# Revit family: Vitra-SinkMixer-Minimax S Series-A42091
name_source: partatom
category: Plumbing Fixtures
revit_build: Autodesk Revit 2017 (Build: 20160225_1515(x64)
units: mm (PartAtom-declared; Revit-internal decimal feet)

## family parameters
Cut with Voids When Loaded = No
Host = Face
OmniClass Number = 23.45.55.17
OmniClass Title = Mixing Faucets
Part Type = Normal
Room Calculation Point = No
Round Connector Dimension = Use Diameter
Shared = Yes

## types (1)
- SinkMixer-Vitra-MinimaxS Series-A42091
    Article No. (default) = A42091
    BIMobject category = Sink Mixer
    CW Connection = Yes
    Coating Material = Vitra-Chrome
    Color = Chrome
    Connection Diameter (mm) = 10 mm  [stored 0.0328084 ft]
    Cost = 0 $
    Default Elevation = 850 mm  [stored 2.78871 ft]
    Depth(mm) = 260 mm  [stored 0.853018 ft]
    Design country = Turkey
    HW Connection = Yes
    Height(mm) = 355 mm
    Hot Water Supply (max.) = 80 °C
    Hot Water temperature, factory set to = 38 °C
    IFC Classification = Sanitary Terminal
    Installation instructions = https://cdn.vitra.com.tr
    Main Material = Brass
    Manufacturer = Vitra
    Manufacturer name = Vitra
    Masterformat 2014 Code = 22 40 00
    Masterformat 2014 Description = Plumbing Fixtures
    Min. flow pressure of = 0.5 bar
    Model = A42091
    MountingType = Countertop
    NBS Referans Code = 45-35-70/345
    NBS Referans Description = Water supply fittings for sinks
    Nominal height = 0.000
    Nominal width = 0.000
    Number Of Connections = 2 mm  [stored 0.00656168 ft]
    OmniClass Code = 23.45.55.17
    OmniClass Description = Mixing Faucets
    Product Guid = https://cdn.vitra.com.tr
    Product Properties = Extra Water Saving, Green Building Certification, Energy Saving, Easy İnstallation
    Product SKU = A42091
    Product Type = Sink Mixer
    Product certification = https://vitraglobal.com
    Product data url = https://www.vitraglobal.com
    Product family = Minimax S
    Product group = Minimax S Sink Mixer
    Range of Hot Water Supply = 5 - 65 °C
    Range of flow pressure = 1 - 5 bar
    Technical description = https://www.vitraglobal.com
    Test Pressure = 16 bar
    UNSPSC Code = 301815
    URL = https://vitraglobal.com
    Uniclass 1.4 Code = L725111
    Uniclass 1.4 Description = Sink Mixer
    Uniclass 2.0 Code = Pr_40_30_96_47
    Uniclass 2.0 Description = Kitchen Taps
    Uniclass 2015 Code = Pr_40_20_87_84
    Uniclass 2015 Name = Sink taps
    Uniformat II Code = 22 40 00
    Uniformat II Description = Plumbing Fixture
    Warranty Period (Year) = 10 Years
    Weight Net (kg) = 1,524
    Width(mm) = 134 mm
    Youtube = https://www.youtube.com

note: [stored X ft] marks values corroborated as IEEE doubles in the binary element streams (Revit-internal decimal feet)

## geometry (parser evidence)
native form markers: Sweep x2
no freeform markers — native parametric forms only
